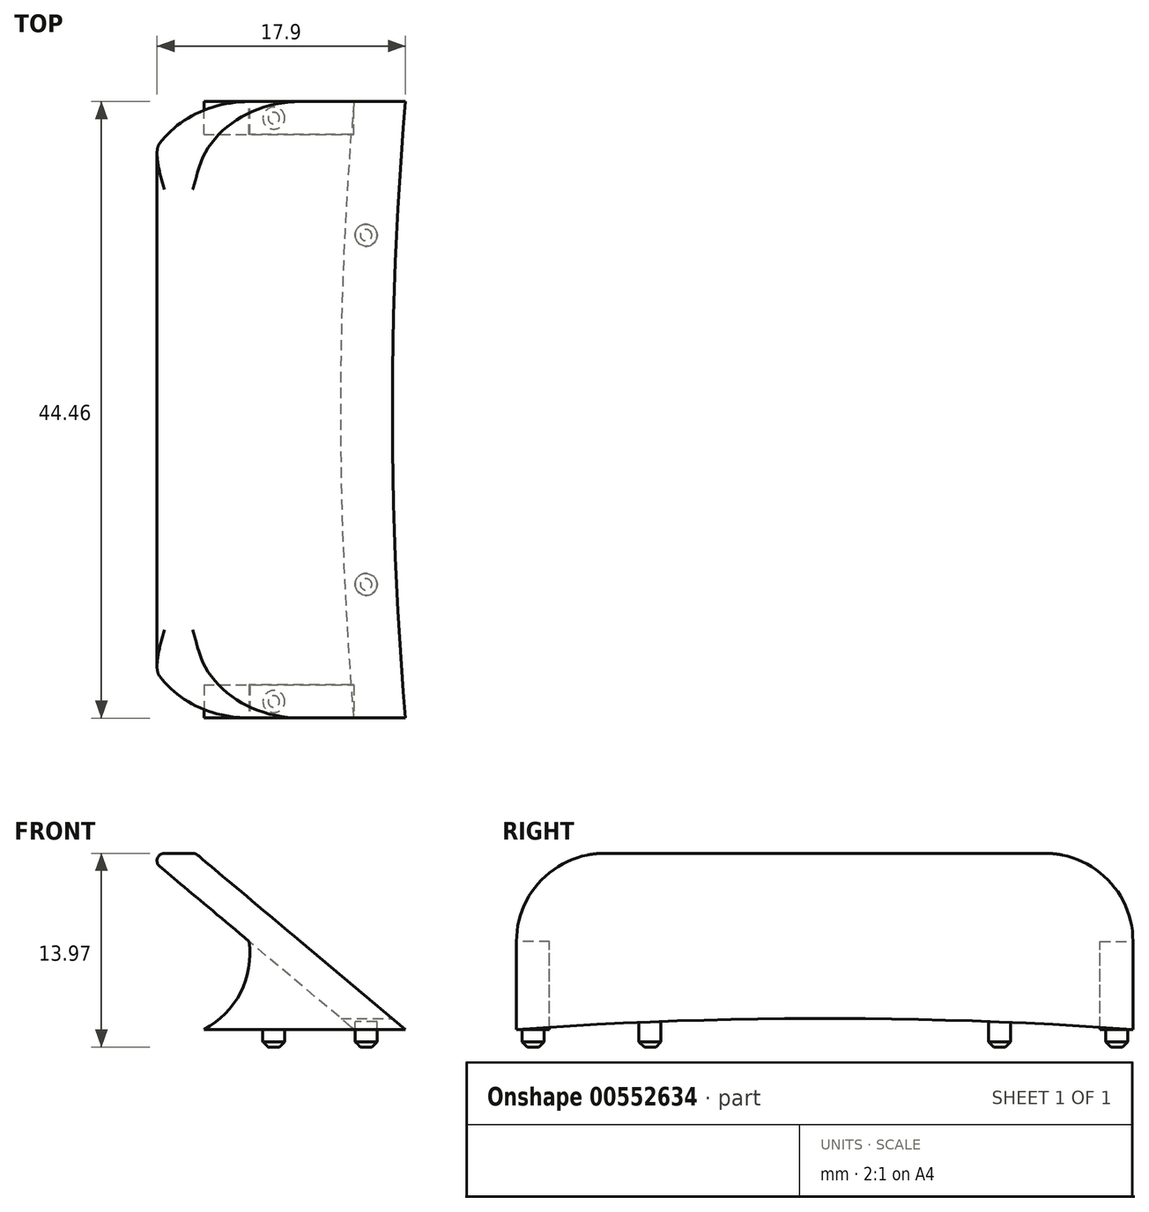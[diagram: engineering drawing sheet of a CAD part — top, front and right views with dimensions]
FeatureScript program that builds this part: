
annotation { "Feature Type Name" : "Feature", "Feature Type Description" : "" }
export const myFeature = defineFeature(function(context is Context, id is Id, definition is map)
    precondition{}
    {
        {
            var Q0;
            Q0=qCreatedBy(makeId("Front.planeOp"),FACE);
            var sketch = newSketch(context, id + "F0", { "sketchPlane" : qUnion([Q0])});
            skLineSegment(sketch, "E0", {"start": v(3.7, 0) * mm, "end": v(0, 0) * mm});
            skLineSegment(sketch, "E1", {"start": v(0, 0) * mm, "end": v(-14, 11.75) * mm});
            skLineSegment(sketch, "E2", {"start": v(-13.66, 12.7) * mm, "end": v(-11.63, 12.7) * mm});
            skLineSegment(sketch, "E3", {"start": v(-11.28, 12.57) * mm, "end": v(3.7, 0) * mm});
            skLineSegment(sketch, "E4", {"start": v(-29.57, 0) * mm, "end": v(35.44, 0) * mm, "construction": true});
            skPoint(sketch, "E5.visualSharp", {"position": v(-15.14, 12.7) * mm});
            skArc(sketch, "E5.filletArc", {"start": v(-13.66, 12.7) * mm, "mid": v(-14.17, 12.35) * mm, "end": v(-14, 11.75) * mm});
            skPoint(sketch, "E6.visualSharp", {"position": v(-11.43, 12.7) * mm});
            skArc(sketch, "E6.filletArc", {"start": v(-11.28, 12.57) * mm, "mid": v(-11.44, 12.67) * mm, "end": v(-11.63, 12.7) * mm});
            skSolve(sketch);
        }
        {
            var Q0;
            Q0 = qSketchRegion(id + "F0", true);
            extrude(context, id + "F1", {"entities" : qUnion([Q0]), "endBound" : BoundingType.SYMMETRIC, "depth" : 44.45 * mm, "offsetDistance" : 25.4 * mm});
        }
        {
            var Q0;
            Q0=qCreatedBy(makeId("Right.planeOp"),FACE);
            var sketch = newSketch(context, id + "F2", { "sketchPlane" : qUnion([Q0])});
            skLineSegment(sketch, "E7", {"start": v(-23.6, 12.7) * mm, "end": v(27.2, 12.7) * mm, "construction": true});
            skLineSegment(sketch, "E8", {"start": v(-25.6, 0) * mm, "end": v(25.26, 0) * mm, "construction": true});
            skLineSegment(sketch, "E9", {"start": v(0, 23.3) * mm, "end": v(0, -9.74) * mm, "construction": true});
            skLineSegment(sketch, "E10", {"start": v(-22.22, 24.14) * mm, "end": v(-22.22, -6.9) * mm, "construction": true});
            skPoint(sketch, "E11", {"position": v(-15.87, 6.35) * mm});
            skArc(sketch, "E12", {"start": v(-15.87, 12.7) * mm, "mid": v(-20.37, 10.84) * mm, "end": v(-22.22, 6.35) * mm});
            skPoint(sketch, "E13", {"position": v(-22.22, 6.35) * mm});
            skPoint(sketch, "E14", {"position": v(-15.87, 12.7) * mm});
            skLineSegment(sketch, "E15", {"start": v(-22.22, 6.35) * mm, "end": v(-26.88, 8.66) * mm});
            skLineSegment(sketch, "E16", {"start": v(-26.88, 8.66) * mm, "end": v(-25.18, 17.7) * mm});
            skLineSegment(sketch, "E17", {"start": v(-25.18, 17.7) * mm, "end": v(-15.87, 12.7) * mm});
            skLineSegment(sketch, "E18.MirrorCS", {"start": v(26.88, 8.66) * mm, "end": v(25.18, 17.7) * mm});
            skLineSegment(sketch, "E19.MirrorCS", {"start": v(25.18, 17.7) * mm, "end": v(15.87, 12.7) * mm});
            skLineSegment(sketch, "E20.MirrorCS", {"start": v(22.22, 6.35) * mm, "end": v(26.88, 8.66) * mm});
            skArc(sketch, "E21.MirrorCS", {"start": v(15.87, 12.7) * mm, "mid": v(20.37, 10.84) * mm, "end": v(22.22, 6.35) * mm});
            skPoint(sketch, "E22.MirrorP", {"position": v(15.87, 12.7) * mm});
            skPoint(sketch, "E23.MirrorP", {"position": v(22.22, 6.35) * mm});
            skSolve(sketch);
        }
        {
            var Q0;
            Q0 = qSketchRegion(id + "F2", true);
            extrude(context, id + "F3", {"entities" : qUnion([Q0]), "operationType" : NewBodyOperationType.REMOVE, "endBound" : BoundingType.THROUGH_ALL, "oppositeDirection" : true, "depth" : 25.4 * mm, "offsetDistance" : 25.4 * mm});
        }
        {
            var Q0;
            Q0=qCreatedBy(makeId("Right.planeOp"),FACE);
            var sketch = newSketch(context, id + "F4", { "sketchPlane" : qUnion([Q0])});
            skLineSegment(sketch, "E24", {"start": v(-23.84, 0) * mm, "end": v(24.2, 0) * mm, "construction": true});
            skLineSegment(sketch, "E25", {"start": v(-23.84, 0.8) * mm, "end": v(23.21, 0.8) * mm, "construction": true});
            skLineSegment(sketch, "E26", {"start": v(0, 7.81) * mm, "end": v(0, -2.5) * mm, "construction": true});
            skPoint(sketch, "E27", {"position": v(0, 0.8) * mm});
            skLineSegment(sketch, "E28", {"start": v(-22.23, -1.57) * mm, "end": v(-22.23, 8.8) * mm, "construction": true});
            skLineSegment(sketch, "E29", {"start": v(22.23, 10.91) * mm, "end": v(22.23, -7.18) * mm, "construction": true});
            skPoint(sketch, "E30", {"position": v(22.23, 0) * mm});
            skPoint(sketch, "E31", {"position": v(-22.23, 0) * mm});
            skCircle(sketch, "E32", {"center": v(0, -310.75) * mm, "radius": 311.55 * mm});
            skSolve(sketch);
        }
        {
            var Q0;
            Q0 = qSketchRegion(id + "F4", true);
            extrude(context, id + "F5", {"entities" : qUnion([Q0]), "operationType" : NewBodyOperationType.REMOVE, "endBound" : BoundingType.SYMMETRIC, "oppositeDirection" : true, "depth" : 76.2 * mm, "offsetDistance" : 25.4 * mm});
        }
        {
            var Q0;
            Q0=makeQuery(id+"F1.opExtrude","CAP_FACE",FACE,{"disambiguationData":[OSD([sQuery(id+"F0.wireOp",EDGE,"E0"),sQuery(id+"F0.wireOp",EDGE,"E1"),sQuery(id+"F0.wireOp",EDGE,"E2"),sQuery(id+"F0.wireOp",EDGE,"E3"),sQuery(id+"F0.wireOp",EDGE,"E5.filletArc"),sQuery(id+"F0.wireOp",EDGE,"E6.filletArc")])],"isStart":false});
            var sketch = newSketch(context, id + "F6", { "sketchPlane" : qUnion([Q0])});
            skLineSegment(sketch, "E33", {"start": v(0, 0) * mm, "end": v(-7.57, 6.35) * mm});
            skLineSegment(sketch, "E34", {"start": v(-10.82, 0) * mm, "end": v(0, 0) * mm});
            skPoint(sketch, "E35", {"position": v(-8.48, 2.13) * mm});
            skArc(sketch, "E36", {"start": v(-10.82, 0) * mm, "mid": v(-8.18, 2.66) * mm, "end": v(-7.57, 6.35) * mm});
            skSolve(sketch);
        }
        {
            var Q0;
            Q0 = qSketchRegion(id + "F6", true);
            extrude(context, id + "F7", {"entities" : qUnion([Q0]), "operationType" : NewBodyOperationType.ADD, "oppositeDirection" : true, "depth" : 2.38 * mm, "offsetDistance" : 25.4 * mm});
        }
        {
            var Q0;
            Q0=makeQuery(id+"F1.opExtrude","SWEPT_BODY",BODY,{"disambiguationData":[OSD([sQuery(id+"F0.wireOp",EDGE,"E0"),sQuery(id+"F0.wireOp",EDGE,"E1"),sQuery(id+"F0.wireOp",EDGE,"E2"),sQuery(id+"F0.wireOp",EDGE,"E3"),sQuery(id+"F0.wireOp",EDGE,"E5.filletArc"),sQuery(id+"F0.wireOp",EDGE,"E6.filletArc")])]});
            var Q1;
            Q1=qCreatedBy(makeId("Front.planeOp"),FACE);
            mirror(context, id + "F8", {"entities" : qUnion([Q0]), "mirrorPlane" : qUnion([Q1])});
        }
        {
            var Q0;
            Q0=makeQuery(id+"F7.opExtrude","SWEPT_FACE",FACE,{"disambiguationData":[OSD([sQuery(id+"F6.wireOp",EDGE,"E34")])]});
            var sketch = newSketch(context, id + "F9", { "sketchPlane" : qUnion([Q0])});
            skPoint(sketch, "E37", {"position": v(0.87, 12.6) * mm});
            skPoint(sketch, "E38", {"position": v(-5.78, 21.03) * mm});
            skLineSegment(sketch, "E39", {"start": v(-23.87, 0) * mm, "end": v(22.33, 0) * mm, "construction": true});
            skCircle(sketch, "E40", {"center": v(-5.78, 21.03) * mm, "radius": 0.8 * mm});
            skCircle(sketch, "E41", {"center": v(0.87, 12.6) * mm, "radius": 0.8 * mm});
            skCircle(sketch, "E42.MirrorC", {"center": v(0.87, -12.6) * mm, "radius": 0.8 * mm});
            skCircle(sketch, "E43.MirrorC", {"center": v(-5.78, -21.03) * mm, "radius": 0.8 * mm});
            skSolve(sketch);
        }
        {
            var Q0;
            Q0 = qSketchRegion(id + "F9", true);
            extrude(context, id + "F10", {"entities" : qUnion([Q0]), "operationType" : NewBodyOperationType.ADD, "endBound" : BoundingType.SYMMETRIC, "depth" : 2.54 * mm, "offsetDistance" : 25.4 * mm});
        }
        {
            var Q0;
            Q0=makeQuery(id+"F10.opExtrude","CAP_EDGE",EDGE,{"disambiguationData":[OSD([sQuery(id+"F9.wireOp",EDGE,"E41")])],"isStart":false});
            var Q1;
            Q1=makeQuery(id+"F10.opExtrude","CAP_EDGE",EDGE,{"disambiguationData":[OSD([sQuery(id+"F9.wireOp",EDGE,"E40")])],"isStart":false});
            var Q2;
            Q2=makeQuery(id+"F10.opExtrude","CAP_EDGE",EDGE,{"disambiguationData":[OSD([sQuery(id+"F9.wireOp",EDGE,"E42.MirrorC")])],"isStart":false});
            var Q3;
            Q3=makeQuery(id+"F10.opExtrude","CAP_EDGE",EDGE,{"disambiguationData":[OSD([sQuery(id+"F9.wireOp",EDGE,"E43.MirrorC")])],"isStart":false});
            chamfer(context, id + "F11", {"entities" : qUnion([Q0, Q1, Q2, Q3]), "width" : 0.38 * mm, "tangentPropagation" : true});
        }
    });
